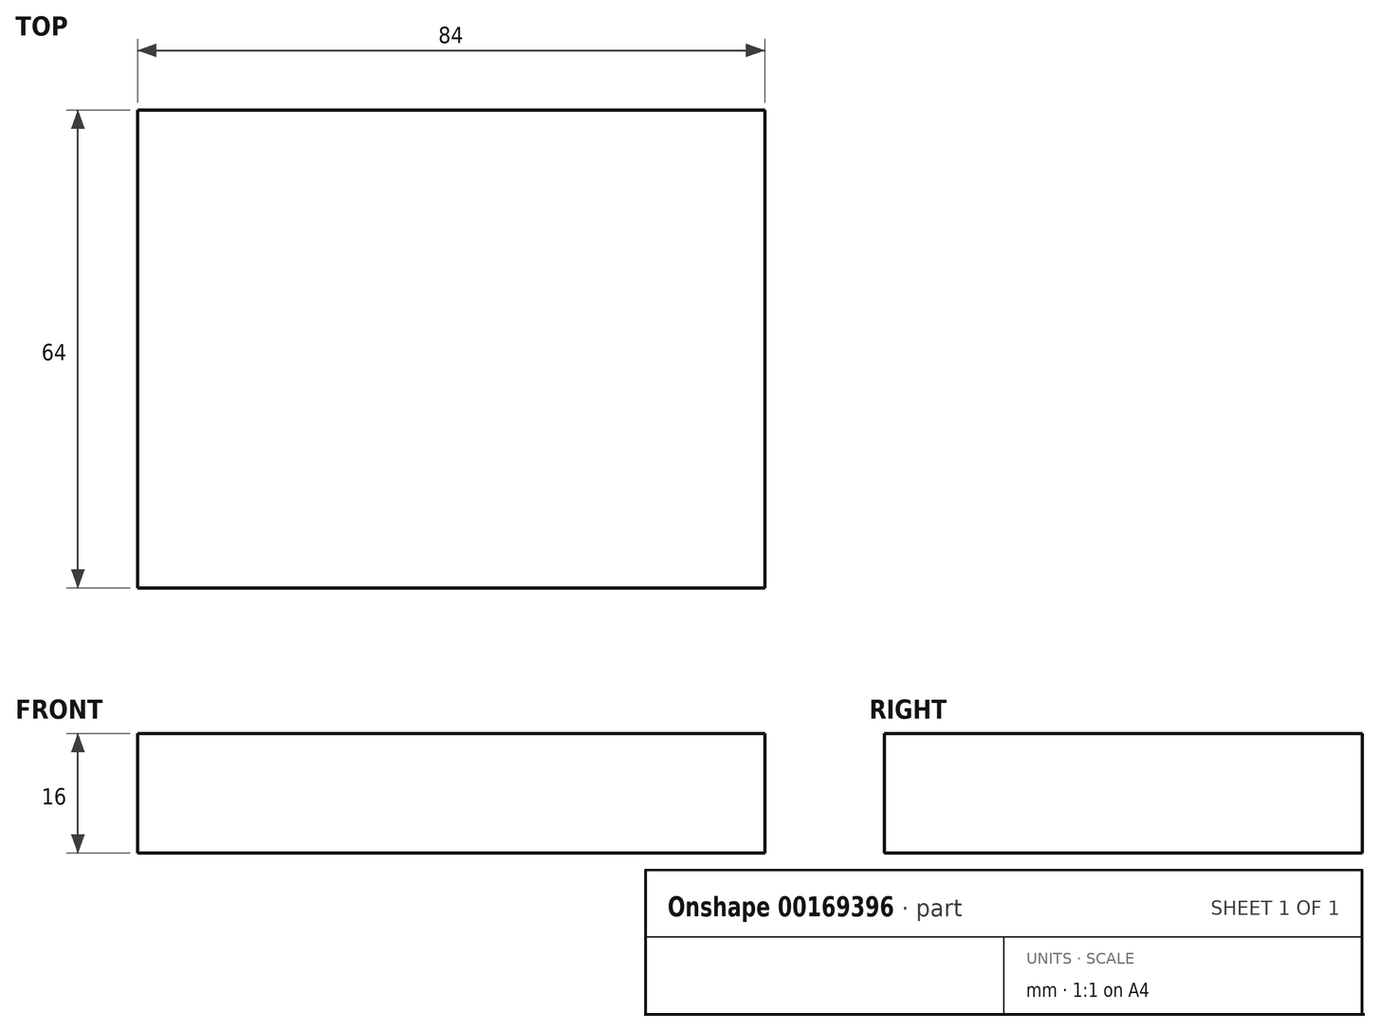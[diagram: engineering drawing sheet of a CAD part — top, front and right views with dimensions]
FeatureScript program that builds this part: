
annotation { "Feature Type Name" : "Feature", "Feature Type Description" : "" }
export const myFeature = defineFeature(function(context is Context, id is Id, definition is map)
    precondition{}
    {
        {
            var Q0;
            Q0=qCreatedBy(makeId("Top.planeOp"),FACE);
            var sketch = newSketch(context, id + "F0", { "sketchPlane" : qUnion([Q0])});
            skLineSegment(sketch, "E0.bottom", {"start": v(42, 32) * mm, "end": v(-42, 32) * mm});
            skLineSegment(sketch, "E0.top", {"start": v(42, -32) * mm, "end": v(-42, -32) * mm});
            skLineSegment(sketch, "E0.left", {"start": v(42, 32) * mm, "end": v(42, -32) * mm});
            skLineSegment(sketch, "E0.right", {"start": v(-42, 32) * mm, "end": v(-42, -32) * mm});
            skPoint(sketch, "E0.middle", {"position": v(0, 0) * mm});
            skSolve(sketch);
        }
        {
            var Q0;
            Q0=makeQuery(id+"F0.imprint","IMPRINT",FACE,{"disambiguationData":[TD([[makeQuery(id+"F0.imprint","IMPRINT",EDGE,{"derivedFrom":sQuery(id+"F0.wireOp",EDGE,"E0.bottom")}),1.0]])]});
            extrude(context, id + "F1", {"entities" : qUnion([Q0]), "depth" : 16 * mm});
        }
    });
